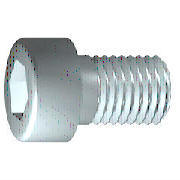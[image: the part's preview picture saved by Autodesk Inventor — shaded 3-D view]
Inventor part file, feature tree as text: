
AUTODESK INVENTOR PART (.ipt)
format: ipt  version: 2016 (Build 200138000, 138)  size: 195,584 bytes
history: native  units: mm (DEFAULTED — no unit token found)
features: sketch x2, extrude x1, plane x1, fillet x1
ambient origin geometry x7: Origin, YZ Plane, XY Plane, X Axis, Y Axis, Z Axis, Center Point
bodies: Solid1 (feature_tree), Body (feature_tree)
feature tree (5):
  extrude  "Slot"  Depth=6.0mm
  plane  "Work Plane1"
  fillet  "Fillet2"  Radius=6.0mm
  sketch  "Sketch1"  dims[d1=7.5mm d2=0.61355mm d3=6.0mm]
  sketch  "Sketch2"  dims[d4=3.0mm d5=60.0deg d6=6.0mm d7=6.0mm d8=5.773503mm d9=10.0mm d10=90.0deg d11=10.0mm d12=0.0mm d13=7.5mm d14=0.0mm d15=0.61345mm d16=0.61345mm d17=0.6mm d19=0.0mm d26=10.0mm d27=45.0deg d28=0.0mm d29=0.0mm d30=0.1mm]
